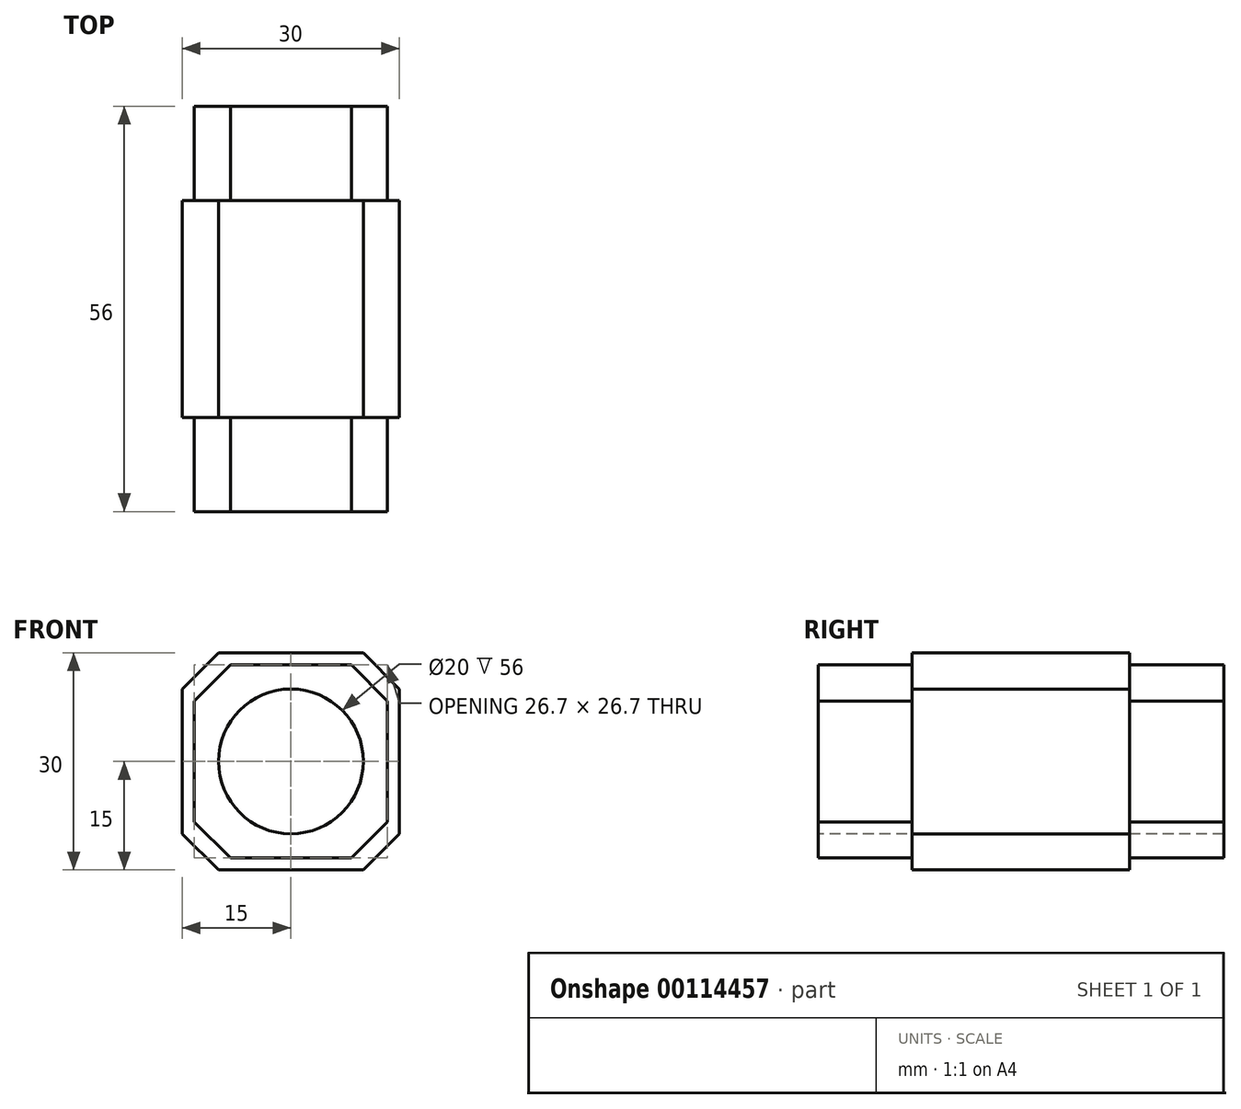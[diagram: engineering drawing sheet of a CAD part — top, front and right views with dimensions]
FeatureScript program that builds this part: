
annotation { "Feature Type Name" : "Feature", "Feature Type Description" : "" }
export const myFeature = defineFeature(function(context is Context, id is Id, definition is map)
    precondition{}
    {
        {
            var Q0;
            Q0=qCreatedBy(makeId("Front.planeOp"),FACE);
            var sketch = newSketch(context, id + "F0", { "sketchPlane" : qUnion([Q0])});
            skLineSegment(sketch, "E0.bottom", {"start": v(13.35, -13.35) * mm, "end": v(-13.35, -13.35) * mm});
            skLineSegment(sketch, "E0.top", {"start": v(13.35, 13.35) * mm, "end": v(-13.35, 13.35) * mm});
            skLineSegment(sketch, "E0.left", {"start": v(13.35, -13.35) * mm, "end": v(13.35, 13.35) * mm});
            skLineSegment(sketch, "E0.right", {"start": v(-13.35, -13.35) * mm, "end": v(-13.35, 13.35) * mm});
            skPoint(sketch, "E0.middle", {"position": v(0, 0) * mm});
            skSolve(sketch);
        }
        {
            var Q0;
            Q0=makeQuery(id+"F0.imprint","IMPRINT",FACE,{"disambiguationData":[TD([[makeQuery(id+"F0.imprint","IMPRINT",EDGE,{"derivedFrom":sQuery(id+"F0.wireOp",EDGE,"E0.bottom")}),-1.0]])]});
            extrude(context, id + "F1", {"entities" : qUnion([Q0]), "endBound" : BoundingType.SYMMETRIC, "depth" : 13 * mm});
        }
        {
            var Q0;
            Q0=makeQuery(id+"F1.opExtrude","CAP_FACE",FACE,{"disambiguationData":[OSD([sQuery(id+"F0.wireOp",EDGE,"E0.bottom"),sQuery(id+"F0.wireOp",EDGE,"E0.top"),sQuery(id+"F0.wireOp",EDGE,"E0.left"),sQuery(id+"F0.wireOp",EDGE,"E0.right")])],"isStart":false});
            var sketch = newSketch(context, id + "F2", { "sketchPlane" : qUnion([Q0])});
            skLineSegment(sketch, "E1.bottom", {"start": v(15, -15) * mm, "end": v(-15, -15) * mm});
            skLineSegment(sketch, "E1.top", {"start": v(15, 15) * mm, "end": v(-15, 15) * mm});
            skLineSegment(sketch, "E1.left", {"start": v(15, -15) * mm, "end": v(15, 15) * mm});
            skLineSegment(sketch, "E1.right", {"start": v(-15, -15) * mm, "end": v(-15, 15) * mm});
            skPoint(sketch, "E1.middle", {"position": v(0, 0) * mm});
            skSolve(sketch);
        }
        {
            var Q0;
            Q0 = qSketchRegion(id + "F2", true);
            extrude(context, id + "F3", {"entities" : qUnion([Q0]), "operationType" : NewBodyOperationType.ADD, "depth" : 30 * mm});
        }
        {
            var Q0;
            Q0=makeQuery(id+"F3.opExtrude","CAP_FACE",FACE,{"disambiguationData":[OSD([sQuery(id+"F2.wireOp",EDGE,"E1.bottom"),sQuery(id+"F2.wireOp",EDGE,"E1.top"),sQuery(id+"F2.wireOp",EDGE,"E1.left"),sQuery(id+"F2.wireOp",EDGE,"E1.right")])],"isStart":false});
            var sketch = newSketch(context, id + "F4", { "sketchPlane" : qUnion([Q0])});
            skLineSegment(sketch, "E2.bottom", {"start": v(13.35, -13.35) * mm, "end": v(-13.35, -13.35) * mm});
            skLineSegment(sketch, "E2.top", {"start": v(13.35, 13.35) * mm, "end": v(-13.35, 13.35) * mm});
            skLineSegment(sketch, "E2.left", {"start": v(13.35, -13.35) * mm, "end": v(13.35, 13.35) * mm});
            skLineSegment(sketch, "E2.right", {"start": v(-13.35, -13.35) * mm, "end": v(-13.35, 13.35) * mm});
            skPoint(sketch, "E2.middle", {"position": v(0, 0) * mm});
            skSolve(sketch);
        }
        {
            var Q0;
            Q0=makeQuery(id+"F4.imprint","IMPRINT",FACE,{"disambiguationData":[TD([[makeQuery(id+"F4.imprint","IMPRINT",EDGE,{"derivedFrom":sQuery(id+"F4.wireOp",EDGE,"E2.bottom")}),-1.0]])]});
            extrude(context, id + "F5", {"entities" : qUnion([Q0]), "operationType" : NewBodyOperationType.ADD, "depth" : 13 * mm});
        }
        {
            var Q0;
            Q0=makeQuery(id+"F5.opExtrude","SWEPT_EDGE",EDGE,{"disambiguationData":[OSD([sQuery(id+"F4.wireOp",EDGE,"E2.top"),sQuery(id+"F4.wireOp",EDGE,"E2.left")])]});
            var Q1;
            Q1=makeQuery(id+"F1.opExtrude","SWEPT_EDGE",EDGE,{"disambiguationData":[OSD([sQuery(id+"F0.wireOp",EDGE,"E0.top"),sQuery(id+"F0.wireOp",EDGE,"E0.left")])]});
            var Q2;
            Q2=makeQuery(id+"F5.opExtrude","SWEPT_EDGE",EDGE,{"disambiguationData":[OSD([sQuery(id+"F4.wireOp",EDGE,"E2.bottom"),sQuery(id+"F4.wireOp",EDGE,"E2.left")])]});
            var Q3;
            Q3=makeQuery(id+"F1.opExtrude","SWEPT_EDGE",EDGE,{"disambiguationData":[OSD([sQuery(id+"F0.wireOp",EDGE,"E0.bottom"),sQuery(id+"F0.wireOp",EDGE,"E0.left")])]});
            var Q4;
            Q4=makeQuery(id+"F5.opExtrude","SWEPT_EDGE",EDGE,{"disambiguationData":[OSD([sQuery(id+"F4.wireOp",EDGE,"E2.top"),sQuery(id+"F4.wireOp",EDGE,"E2.right")])]});
            var Q5;
            Q5=makeQuery(id+"F5.opExtrude","SWEPT_EDGE",EDGE,{"disambiguationData":[OSD([sQuery(id+"F4.wireOp",EDGE,"E2.bottom"),sQuery(id+"F4.wireOp",EDGE,"E2.right")])]});
            var Q6;
            Q6=makeQuery(id+"F1.opExtrude","SWEPT_EDGE",EDGE,{"disambiguationData":[OSD([sQuery(id+"F0.wireOp",EDGE,"E0.bottom"),sQuery(id+"F0.wireOp",EDGE,"E0.right")])]});
            var Q7;
            Q7=makeQuery(id+"F1.opExtrude","SWEPT_EDGE",EDGE,{"disambiguationData":[OSD([sQuery(id+"F0.wireOp",EDGE,"E0.top"),sQuery(id+"F0.wireOp",EDGE,"E0.right")])]});
            var Q8;
            Q8=makeQuery(id+"F3.opExtrude","SWEPT_EDGE",EDGE,{"disambiguationData":[OSD([sQuery(id+"F2.wireOp",EDGE,"E1.top"),sQuery(id+"F2.wireOp",EDGE,"E1.left")])]});
            var Q9;
            Q9=makeQuery(id+"F3.opExtrude","SWEPT_EDGE",EDGE,{"disambiguationData":[OSD([sQuery(id+"F2.wireOp",EDGE,"E1.top"),sQuery(id+"F2.wireOp",EDGE,"E1.right")])]});
            var Q10;
            Q10=makeQuery(id+"F3.opExtrude","SWEPT_EDGE",EDGE,{"disambiguationData":[OSD([sQuery(id+"F2.wireOp",EDGE,"E1.bottom"),sQuery(id+"F2.wireOp",EDGE,"E1.left")])]});
            var Q11;
            Q11=makeQuery(id+"F3.opExtrude","SWEPT_EDGE",EDGE,{"disambiguationData":[OSD([sQuery(id+"F2.wireOp",EDGE,"E1.bottom"),sQuery(id+"F2.wireOp",EDGE,"E1.right")])]});
            chamfer(context, id + "F6", {"entities" : qUnion([Q0, Q1, Q2, Q3, Q4, Q5, Q6, Q7, Q8, Q9, Q10, Q11]), "width" : 5 * mm, "tangentPropagation" : true});
        }
        {
            var Q0;
            Q0=makeQuery(id+"F5.opExtrude","CAP_FACE",FACE,{"disambiguationData":[OSD([sQuery(id+"F4.wireOp",EDGE,"E2.bottom"),sQuery(id+"F4.wireOp",EDGE,"E2.top"),sQuery(id+"F4.wireOp",EDGE,"E2.left"),sQuery(id+"F4.wireOp",EDGE,"E2.right")])],"isStart":false});
            var sketch = newSketch(context, id + "F7", { "sketchPlane" : qUnion([Q0])});
            skCircle(sketch, "E3", {"center": v(0, 0) * mm, "radius": 10 * mm});
            skSolve(sketch);
        }
        {
            var Q0;
            Q0=makeQuery(id+"F7.imprint","IMPRINT",FACE,{"disambiguationData":[TD([[makeQuery(id+"F7.imprint","IMPRINT",EDGE,{"derivedFrom":sQuery(id+"F7.wireOp",EDGE,"E3")}),1.0]])]});
            extrude(context, id + "F8", {"entities" : qUnion([Q0]), "operationType" : NewBodyOperationType.REMOVE, "endBound" : BoundingType.THROUGH_ALL, "oppositeDirection" : true, "depth" : 25 * mm});
        }
    });
